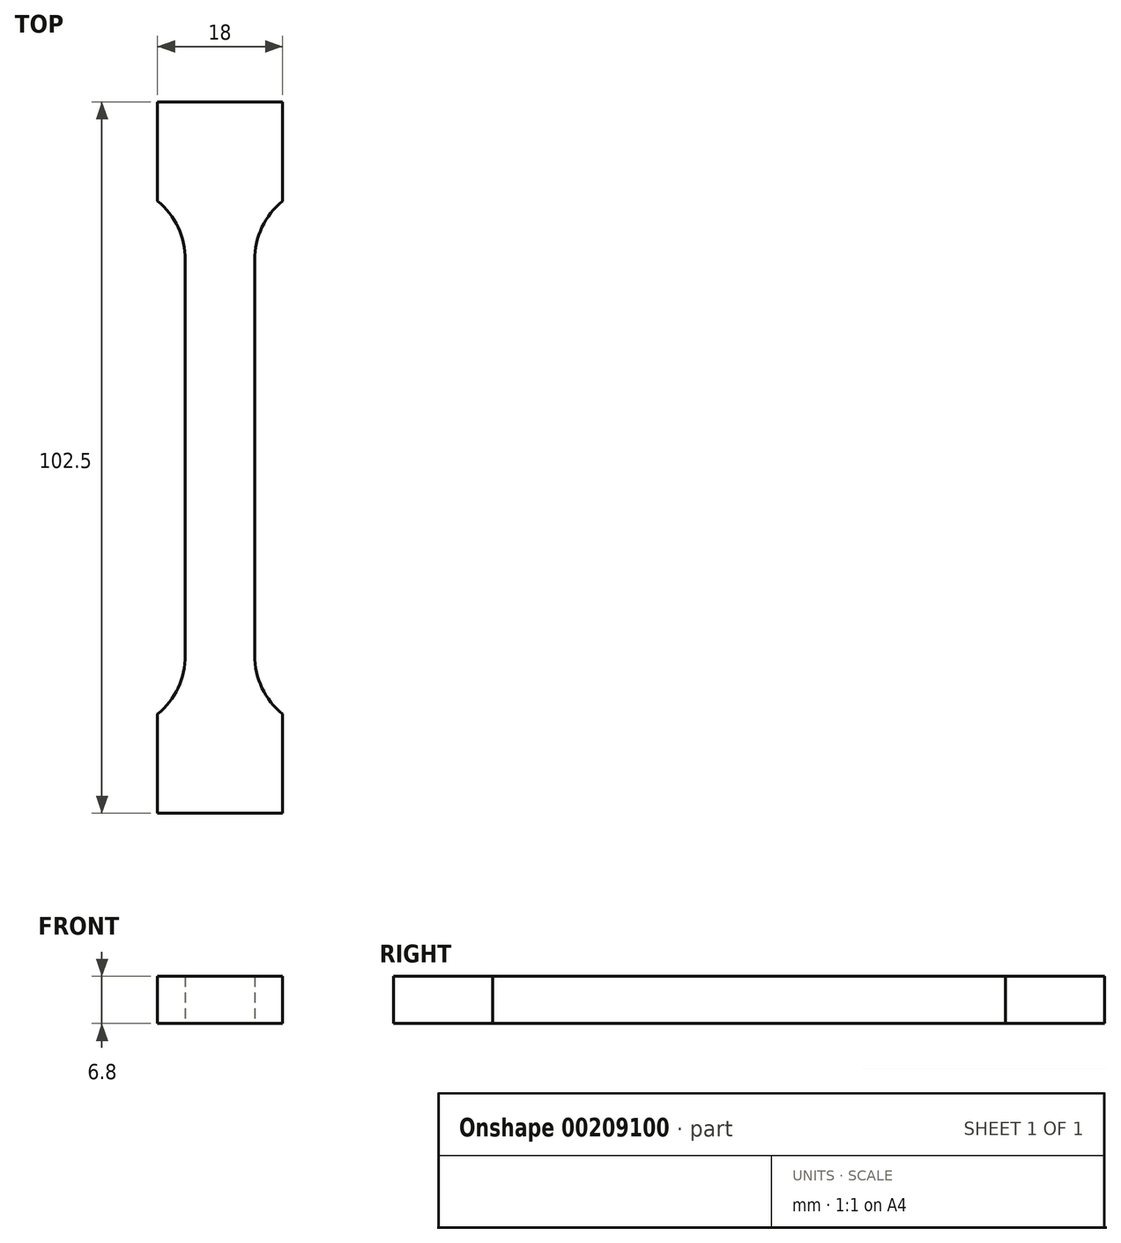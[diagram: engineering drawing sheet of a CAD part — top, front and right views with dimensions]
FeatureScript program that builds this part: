
annotation { "Feature Type Name" : "Feature", "Feature Type Description" : "" }
export const myFeature = defineFeature(function(context is Context, id is Id, definition is map)
    precondition{}
    {
        {
            var Q0;
            Q0=qCreatedBy(makeId("Top.planeOp"),FACE);
            var sketch = newSketch(context, id + "F0", { "sketchPlane" : qUnion([Q0])});
            skArc(sketch, "E0.MirrorCS", {"start": v(25.68, 73.46) * mm, "mid": v(24.63, 78.15) * mm, "end": v(21.68, 81.95) * mm});
            skArc(sketch, "E1.MirrorCS", {"start": v(25.68, 16.46) * mm, "mid": v(24.63, 11.77) * mm, "end": v(21.68, 7.98) * mm});
            skLineSegment(sketch, "E2.MirrorCS", {"start": v(35.68, 16.46) * mm, "end": v(35.68, 73.46) * mm});
            skArc(sketch, "E3.MirrorCS", {"start": v(35.68, 73.46) * mm, "mid": v(36.73, 78.15) * mm, "end": v(39.68, 81.95) * mm});
            skLineSegment(sketch, "E4.MirrorCS", {"start": v(21.68, 96.21) * mm, "end": v(39.68, 96.21) * mm});
            skLineSegment(sketch, "E5.MirrorCS", {"start": v(39.68, 7.98) * mm, "end": v(39.68, -6.29) * mm});
            skLineSegment(sketch, "E6.MirrorCS", {"start": v(21.68, 7.98) * mm, "end": v(21.68, -6.29) * mm});
            skArc(sketch, "E7.MirrorCS", {"start": v(35.68, 16.46) * mm, "mid": v(36.73, 11.77) * mm, "end": v(39.68, 7.98) * mm});
            skLineSegment(sketch, "E8.MirrorCS", {"start": v(21.68, -6.29) * mm, "end": v(39.68, -6.29) * mm});
            skLineSegment(sketch, "E9.MirrorCS", {"start": v(39.68, 96.21) * mm, "end": v(39.68, 81.95) * mm});
            skLineSegment(sketch, "E10.MirrorCS", {"start": v(25.68, 16.46) * mm, "end": v(25.68, 73.46) * mm});
            skLineSegment(sketch, "E11.MirrorCS", {"start": v(21.68, 96.21) * mm, "end": v(21.68, 81.95) * mm});
            skSolve(sketch);
        }
        {
            var Q0;
            Q0=makeQuery(id+"F0.imprint","IMPRINT",FACE,{"disambiguationData":[TD([[makeQuery(id+"F0.imprint","IMPRINT",EDGE,{"derivedFrom":sQuery(id+"F0.wireOp",EDGE,"E0.MirrorCS")}),-1.0]])]});
            extrude(context, id + "F1", {"entities" : qUnion([Q0]), "depth" : 6.8 * mm, "symmetric" : true});
        }
    });
